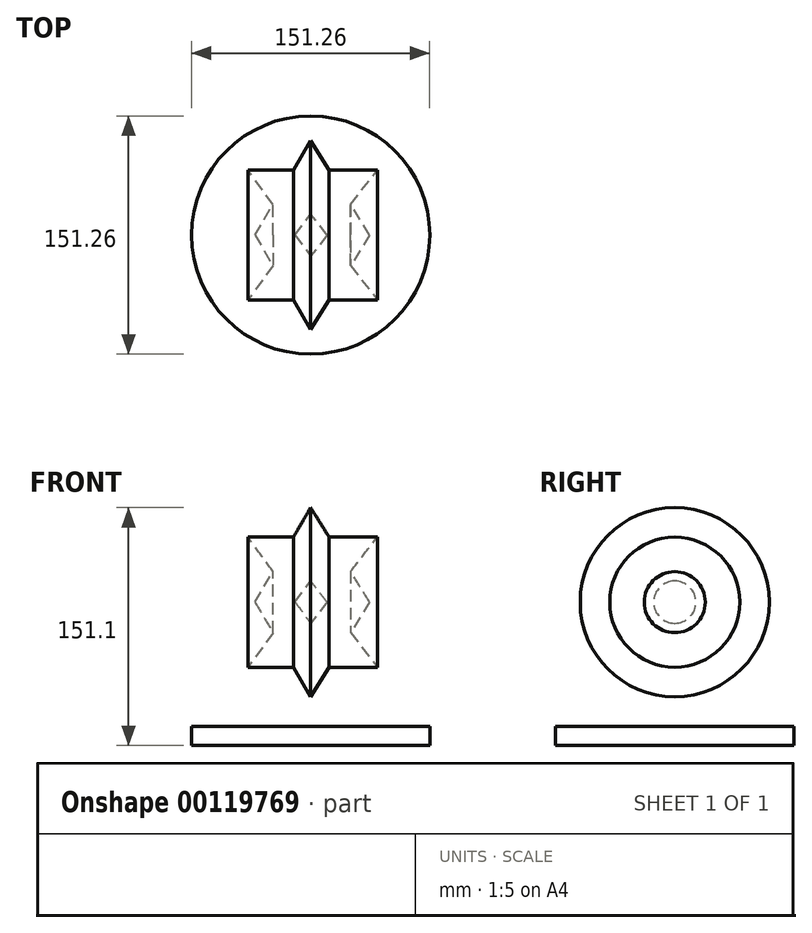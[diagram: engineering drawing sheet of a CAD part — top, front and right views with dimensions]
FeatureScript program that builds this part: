
annotation { "Feature Type Name" : "Feature", "Feature Type Description" : "" }
export const myFeature = defineFeature(function(context is Context, id is Id, definition is map)
    precondition{}
    {
        {
            var Q0;
            Q0=qCreatedBy(makeId("Front.planeOp"),FACE);
            var sketch = newSketch(context, id + "F0", { "sketchPlane" : qUnion([Q0])});
            skLineSegment(sketch, "E0", {"start": v(0, 54.71) * mm, "end": v(-39.93, 0) * mm});
            skLineSegment(sketch, "E1", {"start": v(-39.93, 0) * mm, "end": v(42.37, 0) * mm});
            skLineSegment(sketch, "E2", {"start": v(42.37, 0) * mm, "end": v(0, 54.71) * mm});
            skLineSegment(sketch, "E3", {"start": v(-35.36, 41.3) * mm, "end": v(37.5, 41.3) * mm});
            skLineSegment(sketch, "E4", {"start": v(37.5, 41.3) * mm, "end": v(0, -18.75) * mm});
            skLineSegment(sketch, "E5", {"start": v(0, -18.75) * mm, "end": v(-35.36, 41.3) * mm});
            skSolve(sketch);
        }
        {
            var Q0;
            Q0 = qSketchRegion(id + "F0", true);
            var Q1;
            Q1=sQuery(id+"F0.wireOp",EDGE,"E3");
            revolve(context, id + "F1", {"entities" : qUnion([Q0]), "axis" : qUnion([Q1]), "revolveType" : RevolveType.FULL});
        }
        {
            var Q0;
            Q0=qCreatedBy(makeId("Front.planeOp"),FACE);
            var sketch = newSketch(context, id + "F2", { "sketchPlane" : qUnion([Q0])});
            skLineSegment(sketch, "E6.bottom", {"start": v(0, -37.67) * mm, "end": v(-75.63, -37.67) * mm});
            skLineSegment(sketch, "E6.top", {"start": v(0, -49.75) * mm, "end": v(-75.63, -49.75) * mm});
            skLineSegment(sketch, "E6.left", {"start": v(0, -37.67) * mm, "end": v(0, -49.75) * mm});
            skLineSegment(sketch, "E6.right", {"start": v(-75.63, -37.67) * mm, "end": v(-75.63, -49.75) * mm});
            skSolve(sketch);
        }
        {
            var Q0;
            Q0 = qSketchRegion(id + "F2", true);
            var Q1;
            Q1=sQuery(id+"F2.wireOp",EDGE,"E6.left");
            revolve(context, id + "F3", {"entities" : qUnion([Q0]), "axis" : qUnion([Q1]), "revolveType" : RevolveType.FULL});
        }
    });
